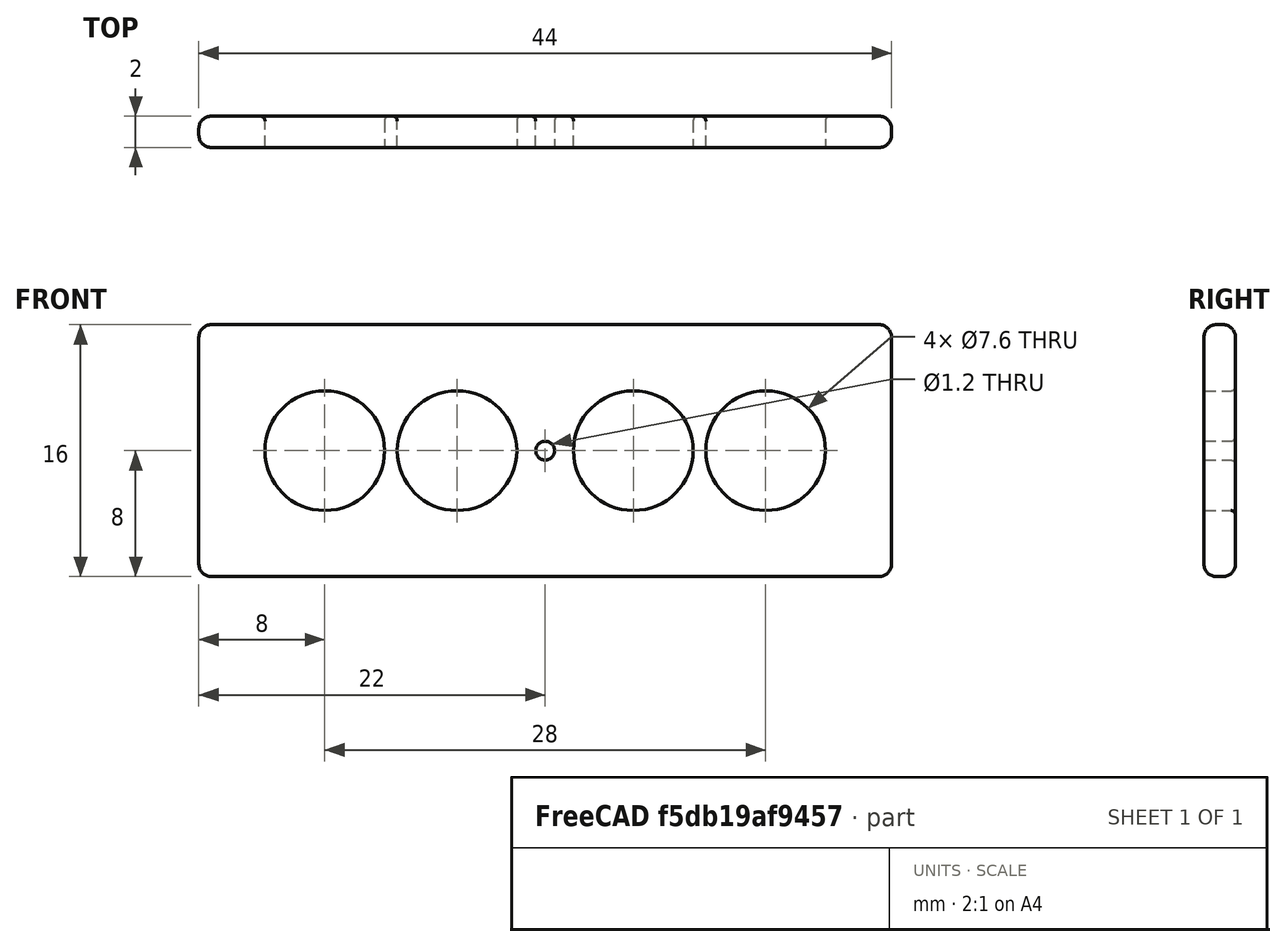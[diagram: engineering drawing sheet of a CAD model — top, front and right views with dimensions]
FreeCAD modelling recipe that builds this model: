
FCSTD DOCUMENT  (FreeCAD 0.16R6712 (Git))
Label: top4
License: All rights reserved
LicenseURL: http://en.wikipedia.org/wiki/All_rights_reserved
objects: Sketcher::SketchObject×2, PartDesign::Fillet×2, PartDesign::Pad×1, PartDesign::Pocket×1, Mesh::Feature×1
note: 8 computed .brp shape members not serialized (recipe doc carries the construction recipe); baked Part::Feature solids carry a one-line shape summary decoded from their .brp

FEATURE [Sketcher::SketchObject] Sketch001
  Placement = pos=(0,-3,0) rot=(1,0,0;1.5708rad)
  sketch-geometry (4):
    g0: LineSegment StartX=-22 StartY=8 StartZ=0 EndX=22 EndY=8 EndZ=0
    g1: LineSegment StartX=22 StartY=8 StartZ=0 EndX=22 EndY=-8 EndZ=0
    g2: LineSegment StartX=22 StartY=-8 StartZ=0 EndX=-22 EndY=-8 EndZ=0
    g3: LineSegment StartX=-22 StartY=-8 StartZ=0 EndX=-22 EndY=8 EndZ=0
  constraints (12):
    c: Coincident(g0,g1)
    c: Coincident(g1,g2)
    c: Coincident(g2,g3)
    c: Coincident(g3,g0)
    c: Horizontal(g0)
    c: Horizontal(g2)
    c: Vertical(g1)
    c: Vertical(g3)
    c: Symmetric(g0,g0,g-2)
    c: Symmetric(g1,g0,g-1)
    c: DistanceX(g-2,g0) = 22
    c: DistanceY(g-1,g0) = 8
FEATURE [PartDesign::Pad] Pad
  Length = 2
  Length2 = 100
  Placement = pos=(0,-3,0) rot=(1,0,0;1.5708rad)
  Sketch = -> Sketch001
  Type = 0
FEATURE [PartDesign::Fillet] Fillet
  Base = -> Pad [Edge4,Edge7,Edge10,Edge12,Edge5,Edge8,Edge9,Edge1,Edge11,Edge3,Edge6,Edge2]
  Placement = pos=(0,-3,0) rot=(1,0,0;1.5708rad)
  Radius = 0.8
FEATURE [Sketcher::SketchObject] Sketch002
  Placement = pos=(0,-3,0) rot=(-1,0,0;1.5708rad)
  Support = -> Fillet [Face13]
  sketch-geometry (5):
    g0: Circle CenterX=-5.6 CenterY=0 CenterZ=0 NormalX=0 NormalY=0 NormalZ=1 Radius=3.8
    g1: Circle CenterX=-14 CenterY=0 CenterZ=0 NormalX=0 NormalY=0 NormalZ=1 Radius=3.8
    g2: Circle CenterX=5.6 CenterY=0 CenterZ=0 NormalX=0 NormalY=0 NormalZ=1 Radius=3.8
    g3: Circle CenterX=14 CenterY=0 CenterZ=0 NormalX=0 NormalY=0 NormalZ=1 Radius=3.8
    g4: Circle CenterX=0 CenterY=0 CenterZ=0 NormalX=0 NormalY=0 NormalZ=1 Radius=0.6
  constraints (13):
    c: Radius(g3) = 3.8
    c: Equal(g3,g2)
    c: Equal(g0,g1)
    c: PointOnObject(g1,g-1)
    c: PointOnObject(g0,g-1)
    c: PointOnObject(g2,g-1)
    c: PointOnObject(g3,g-1)
    c: DistanceX(g-2,g2) = 5.6
    c: Distance(g2,g3) = 8.4
    c: Symmetric(g0,g2,g-2)
    c: Symmetric(g1,g3,g-2)
    c: Coincident(g4,g-1)
    c: Radius(g4) = 0.6
FEATURE [PartDesign::Pocket] Pocket
  Length = 5
  Placement = pos=(0,-3,0) rot=(1,0,0;1.5708rad)
  Sketch = -> Sketch002
  Type = 0
FEATURE [PartDesign::Fillet] Fillet001
  Base = -> Pocket [Edge46,Edge44,Edge43,Edge42,Edge45]
  Placement = pos=(0,-3,0) rot=(1,0,0;1.5708rad)
  Radius = 0.3
FEATURE [Mesh::Feature] Mesh  label="Fillet001 (Meshed)"
